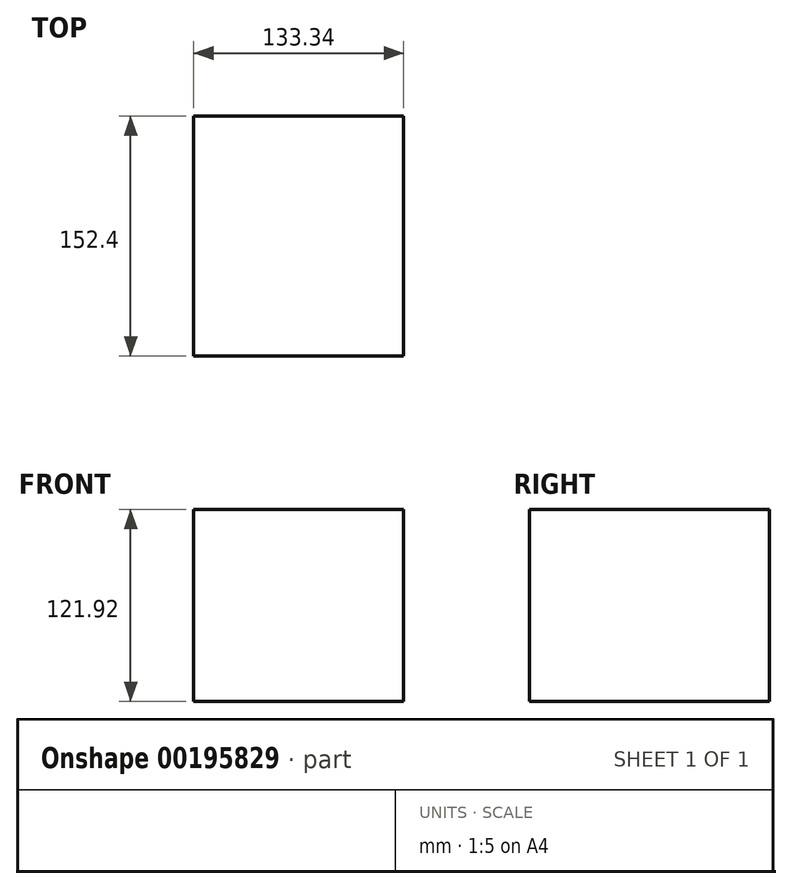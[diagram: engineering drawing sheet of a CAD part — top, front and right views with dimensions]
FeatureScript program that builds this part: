
annotation { "Feature Type Name" : "Feature", "Feature Type Description" : "" }
export const myFeature = defineFeature(function(context is Context, id is Id, definition is map)
    precondition{}
    {
        {
            var Q0;
            Q0=qCreatedBy(makeId("Top.planeOp"),FACE);
            var sketch = newSketch(context, id + "F0", { "sketchPlane" : qUnion([Q0])});
            skLineSegment(sketch, "E0.bottom", {"start": v(-66.67, 76.2) * mm, "end": v(66.68, 76.2) * mm});
            skLineSegment(sketch, "E0.top", {"start": v(-66.68, -76.2) * mm, "end": v(66.67, -76.2) * mm});
            skLineSegment(sketch, "E0.left", {"start": v(-66.67, 76.2) * mm, "end": v(-66.68, -76.2) * mm});
            skLineSegment(sketch, "E0.right", {"start": v(66.68, 76.2) * mm, "end": v(66.67, -76.2) * mm});
            skPoint(sketch, "E0.middle", {"position": v(0, 0) * mm});
            skSolve(sketch);
        }
        {
            var Q0;
            Q0=makeQuery(id+"F0.imprint","IMPRINT",FACE,{"disambiguationData":[TD([[makeQuery(id+"F0.imprint","IMPRINT",EDGE,{"derivedFrom":sQuery(id+"F0.wireOp",EDGE,"E0.bottom")}),-1.0]])]});
            extrude(context, id + "F1", {"entities" : qUnion([Q0]), "depth" : 121.92 * mm});
        }
    });
